# Revit family: KEUCO_14949010200
name_source: partatom
category: Sonderausstattung
revit_build: Autodesk Revit 2016 (Build: 20150220_1215(x64)
units: mm (PartAtom-declared; Revit-internal decimal feet)

## family parameters
Arbeitsebenenbasiert = Nein
Beim Laden mit Abzugskörper schneiden = Nein
Bemaßung runder Anschluss = Durchmesser verwenden
Gemeinsam genutzt = Nein
Immer vertikal = Ja
Raumberechnungspunkt = Nein
Teiletyp = Normal

## types (3) — shared parameters
Gewicht = 382
Hersteller = KEUCO
Kategorie = ACC
Preisgruppe = 1
Serie = Plan
URL = https://www.keuco.com
Verwendung = BI / GWC / WP

## per-type parameters (varying)
| type | Ausschreibungstext |
| 14949010200 | KEUCO PLAN Lotionspender 14949010200 
Einbaumodell zur Untertischmontage
Hochglanzverchromter Lotionspender 
in ästhetischem, funktionalem Design
Einbaumodell, zur verdeckten Untertischmontage 
in Waschtische und Waschtischplatten 
bis zu einer maximalen Stärke von 45 mm,
komplett mit abschraubbarem Untertisch-Kunststoffspender
Befüllen von oben durch rausschrauben der Pumpe
Füllmenge ca. 500 ml, für handelsübliche Flüssigseifen
Dosiermenge ca. 0,5 ml/Hub
Zum Einbau ist eine Bohrung im Waschtisch/in der Waschtischplatte 
von 26.3 mm notwendig, welche nach der Montage durch eine 
verchromte Design-Rosettenkappe verdeckt wird, 
sichtbare Spenderhöhe 92 mm, Ausladung 86 mm |
| 14949070200 | KEUCO PLAN Lotionspender 14949070200 
Einbaumodell zur Untertischmontage
Lotionspender aus hochwertigem Edelstahl 
in ästhetischem, funktionalem Design
Einbaumodell, zur verdeckten Untertischmontage 
in Waschtische und Waschtischplatten 
bis zu einer maximalen Stärke von 45 mm,
komplett mit abschraubbarem Untertisch-Kunststoffspender
Befüllen von oben durch rausschrauben der Pumpe
Füllmenge bis 500 ml, für handelsübliche Flüssigseifen
Dosiermenge ca. 0,5 ml/Hub
Zum Einbau ist eine Bohrung im Waschtisch/in der Waschtischplatte 
von 26.3 mm notwendig, welche nach der Montage durch 
eine verchromte Design-Rosettenkappe verdeckt wird,
sichtbare Spenderhöhe 92 mm, Ausladung 86 mm |
| 14949170200 | KEUCO PLAN Lotionspender 14949170200 
Einbaumodell zur Untertischmontage
Zeitloser Lotionspender aus Aluminium-finish 
in ästhetischem, funktionalem Design
Einbaumodell, zur verdeckten Untertischmontage 
in Waschtische und Waschtischplatten bis zu 
einer maximalen Stärke von 45 mm
komplett mit abschraubbarem Untertisch-Kunststoffspender
Befüllen von oben durch rausschrauben der Pumpe
Füllmenge bis 500 ml, für handelsübliche Flüssigseifen
Dosiermenge ca. 0,5 ml/Hub
Zum Einbau ist eine Bohrung im Waschtisch/in der Waschtischplatte 
von 26.3 mm notwendig, welche nach der Montage 
durch eine verchromte Design-Rosettenkappe verdeckt wird, 
sichtbare Spenderhöhe 92 mm, Ausladung 86 mm |

note: column(s) folded — value = type name in every type: Artikelnummer

## geometry (parser evidence)
native form markers: Blend x4, Sweep x2
no freeform markers — native parametric forms only
